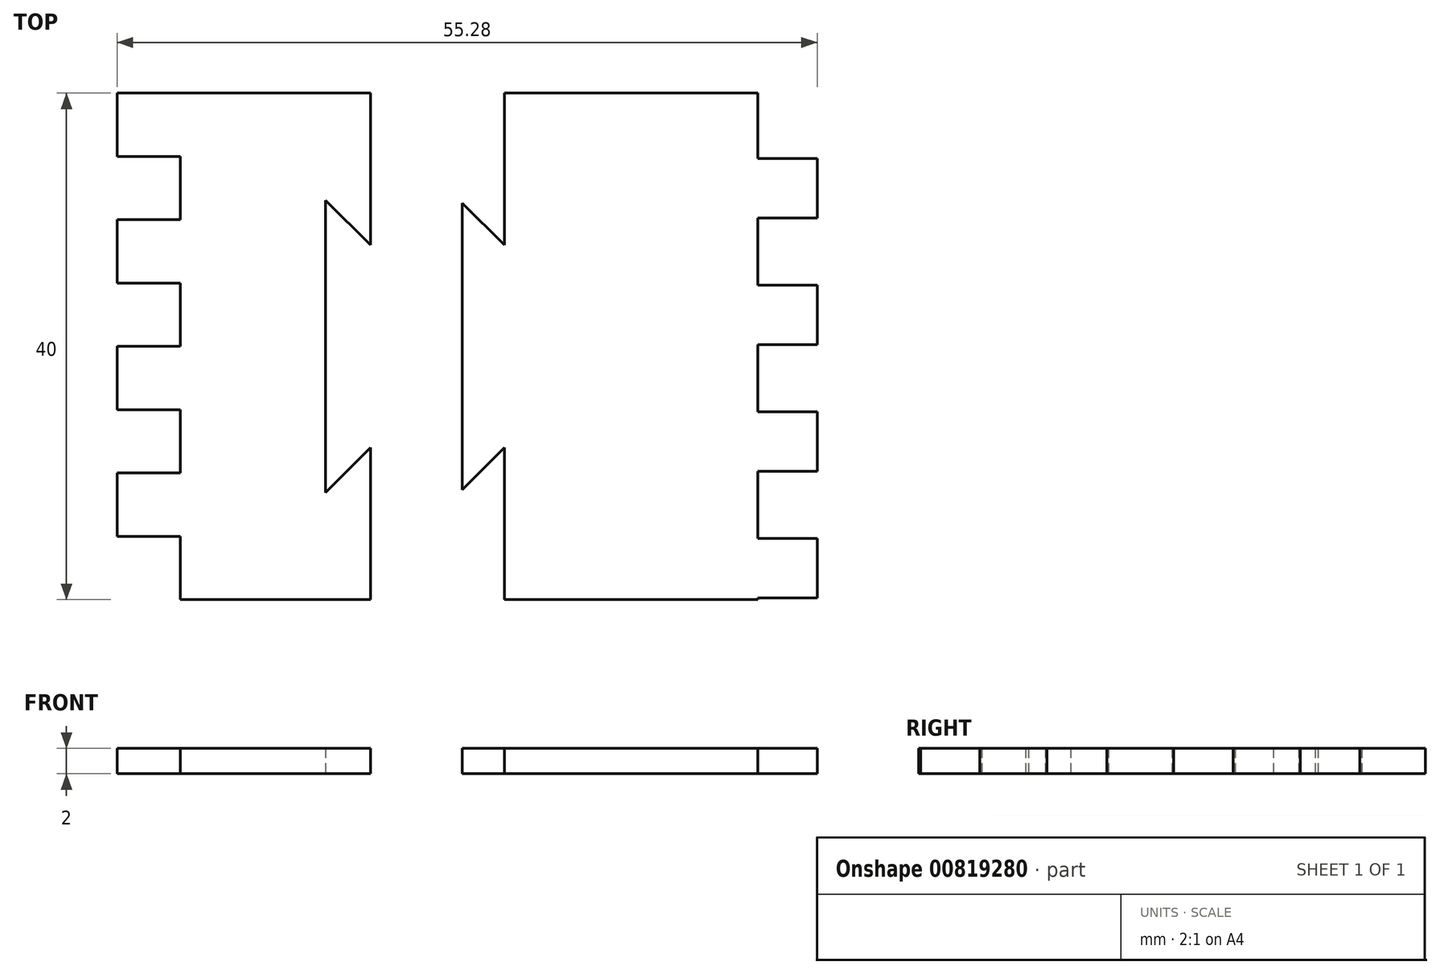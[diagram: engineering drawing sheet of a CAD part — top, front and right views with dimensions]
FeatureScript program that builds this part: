
annotation { "Feature Type Name" : "Feature", "Feature Type Description" : "" }
export const myFeature = defineFeature(function(context is Context, id is Id, definition is map)
    precondition{}
    {
        {
            var Q0;
            Q0=qCreatedBy(makeId("Top.planeOp"),FACE);
            var sketch = newSketch(context, id + "F0", { "sketchPlane" : qUnion([Q0])});
            skLineSegment(sketch, "E0", {"start": v(0, 20) * mm, "end": v(0, 8) * mm});
            skPoint(sketch, "E1", {"position": v(0, 0) * mm});
            skLineSegment(sketch, "E2", {"start": v(0, 20) * mm, "end": v(-20, 20) * mm});
            skLineSegment(sketch, "E3", {"start": v(-20, 20) * mm, "end": v(-20, 15) * mm});
            skLineSegment(sketch, "E4", {"start": v(-15, -20) * mm, "end": v(0, -20) * mm});
            skLineSegment(sketch, "E5", {"start": v(0, 8) * mm, "end": v(-3.54, 11.54) * mm});
            skPoint(sketch, "E6", {"position": v(0, -8) * mm});
            skLineSegment(sketch, "E7", {"start": v(0, -8) * mm, "end": v(-3.54, -11.54) * mm});
            skLineSegment(sketch, "E8", {"start": v(-3.54, 11.54) * mm, "end": v(-3.54, -11.54) * mm});
            skLineSegment(sketch, "E9.trimOffspring", {"start": v(0, -8) * mm, "end": v(0, -20) * mm});
            skLineSegment(sketch, "E10.bottom", {"start": v(10.58, 20) * mm, "end": v(30.58, 20) * mm});
            skLineSegment(sketch, "E10.top", {"start": v(10.58, -20) * mm, "end": v(30.58, -20) * mm});
            skLineSegment(sketch, "E10.left", {"start": v(10.58, 20) * mm, "end": v(10.58, 8) * mm});
            skLineSegment(sketch, "E10.right", {"start": v(30.58, 20) * mm, "end": v(30.58, 14.85) * mm});
            skPoint(sketch, "E11", {"position": v(10.58, 8) * mm});
            skLineSegment(sketch, "E12", {"start": v(10.58, 8) * mm, "end": v(7.25, 11.32) * mm});
            skLineSegment(sketch, "E13", {"start": v(7.25, 11.32) * mm, "end": v(7.25, -11.32) * mm});
            skLineSegment(sketch, "E14", {"start": v(7.25, -11.32) * mm, "end": v(10.58, -8) * mm});
            skLineSegment(sketch, "E15.trimOffspring", {"start": v(10.58, -8) * mm, "end": v(10.58, -20) * mm});
            skLineSegment(sketch, "E16.bottom", {"start": v(-20, 15) * mm, "end": v(-15, 15) * mm});
            skLineSegment(sketch, "E16.top", {"start": v(-20, 10) * mm, "end": v(-15, 10) * mm});
            skLineSegment(sketch, "E16.right", {"start": v(-15, 15) * mm, "end": v(-15, 10) * mm});
            skLineSegment(sketch, "E17.trimOffspring", {"start": v(-20, 10) * mm, "end": v(-20, 5) * mm});
            skLineSegment(sketch, "E18.bottom", {"start": v(-20, 5) * mm, "end": v(-15, 5) * mm});
            skLineSegment(sketch, "E18.top", {"start": v(-20, 0) * mm, "end": v(-15, 0) * mm});
            skLineSegment(sketch, "E18.right", {"start": v(-15, 5) * mm, "end": v(-15, 0) * mm});
            skLineSegment(sketch, "E19.bottom", {"start": v(-20, -5) * mm, "end": v(-15, -5) * mm});
            skLineSegment(sketch, "E19.top", {"start": v(-20, -10) * mm, "end": v(-15, -10) * mm});
            skLineSegment(sketch, "E19.right", {"start": v(-15, -5) * mm, "end": v(-15, -10) * mm});
            skLineSegment(sketch, "E20.top", {"start": v(-20, -15) * mm, "end": v(-15, -15) * mm});
            skLineSegment(sketch, "E20.right", {"start": v(-15, -20) * mm, "end": v(-15, -15) * mm});
            skLineSegment(sketch, "E21.trimOffspring", {"start": v(-20, 0) * mm, "end": v(-20, -5) * mm});
            skLineSegment(sketch, "E22.trimOffspring", {"start": v(-20, -10) * mm, "end": v(-20, -15) * mm});
            skPoint(sketch, "E23", {"position": v(-15, 12.5) * mm});
            skLineSegment(sketch, "E24", {"start": v(35.28, 14.85) * mm, "end": v(35.28, 10.15) * mm});
            skPoint(sketch, "E25", {"position": v(35.28, 12.5) * mm});
            skLineSegment(sketch, "E26", {"start": v(35.28, 14.85) * mm, "end": v(30.58, 14.85) * mm});
            skLineSegment(sketch, "E27", {"start": v(35.28, 10.15) * mm, "end": v(30.58, 10.15) * mm});
            skPoint(sketch, "E28", {"position": v(-15, 2.5) * mm});
            skLineSegment(sketch, "E29.bottom", {"start": v(30.58, 4.85) * mm, "end": v(35.28, 4.85) * mm});
            skLineSegment(sketch, "E29.top", {"start": v(30.58, 0.15) * mm, "end": v(35.28, 0.15) * mm});
            skLineSegment(sketch, "E29.right", {"start": v(35.28, 4.85) * mm, "end": v(35.28, 0.15) * mm});
            skPoint(sketch, "E30", {"position": v(35.28, 2.5) * mm});
            skLineSegment(sketch, "E31.bottom", {"start": v(30.58, -5.15) * mm, "end": v(35.28, -5.15) * mm});
            skLineSegment(sketch, "E31.top", {"start": v(30.58, -9.85) * mm, "end": v(35.28, -9.85) * mm});
            skLineSegment(sketch, "E31.right", {"start": v(35.28, -5.15) * mm, "end": v(35.28, -9.85) * mm});
            skPoint(sketch, "E32", {"position": v(35.28, -7.5) * mm});
            skPoint(sketch, "E33", {"position": v(-15, -7.5) * mm});
            skLineSegment(sketch, "E34.bottom", {"start": v(30.58, -15.15) * mm, "end": v(35.28, -15.15) * mm});
            skLineSegment(sketch, "E34.top", {"start": v(30.58, -19.85) * mm, "end": v(35.28, -19.85) * mm});
            skLineSegment(sketch, "E34.right", {"start": v(35.28, -15.15) * mm, "end": v(35.28, -19.85) * mm});
            skPoint(sketch, "E35", {"position": v(-15, -17.5) * mm});
            skPoint(sketch, "E36", {"position": v(35.28, -17.5) * mm});
            skLineSegment(sketch, "E37.trimOffspring", {"start": v(30.58, 10.15) * mm, "end": v(30.58, 4.85) * mm});
            skLineSegment(sketch, "E38.trimOffspring", {"start": v(30.58, 0.15) * mm, "end": v(30.58, -5.15) * mm});
            skLineSegment(sketch, "E39.trimOffspring", {"start": v(30.58, -9.85) * mm, "end": v(30.58, -15.15) * mm});
            skLineSegment(sketch, "E40.trimOffspring", {"start": v(30.58, -19.85) * mm, "end": v(30.58, -20) * mm});
            skSolve(sketch);
        }
        {
            var Q0;
            {var subQ3=sQuery(id+"F0.wireOp",EDGE,"E10.bottom");Q0=makeQuery(id+"F0.imprint","IMPRINT",FACE,{"disambiguationData":[TD([[makeQuery(id+"F0.imprint","IMPRINT",EDGE,{"derivedFrom":subQ3}),-1.0]])]});}
            var Q1;
            {var subQ0=sQuery(id+"F0.wireOp",EDGE,"E12");Q1=makeQuery(id+"F0.imprint","IMPRINT",FACE,{"disambiguationData":[TD([[makeQuery(id+"F0.imprint","IMPRINT",EDGE,{"derivedFrom":subQ0}),1.0]])]});}
            var Q2;
            Q2=makeQuery(id+"F0.imprint","IMPRINT",FACE,{"disambiguationData":[TD([[makeQuery(id+"F0.imprint","IMPRINT",EDGE,{"derivedFrom":sQuery(id+"F0.wireOp",EDGE,"E0")}),-1.0]])]});
            extrude(context, id + "F1", {"entities" : qUnion([Q0, Q1, Q2]), "depth" : 2 * mm, "offsetDistance" : 25 * mm});
        }
    });
